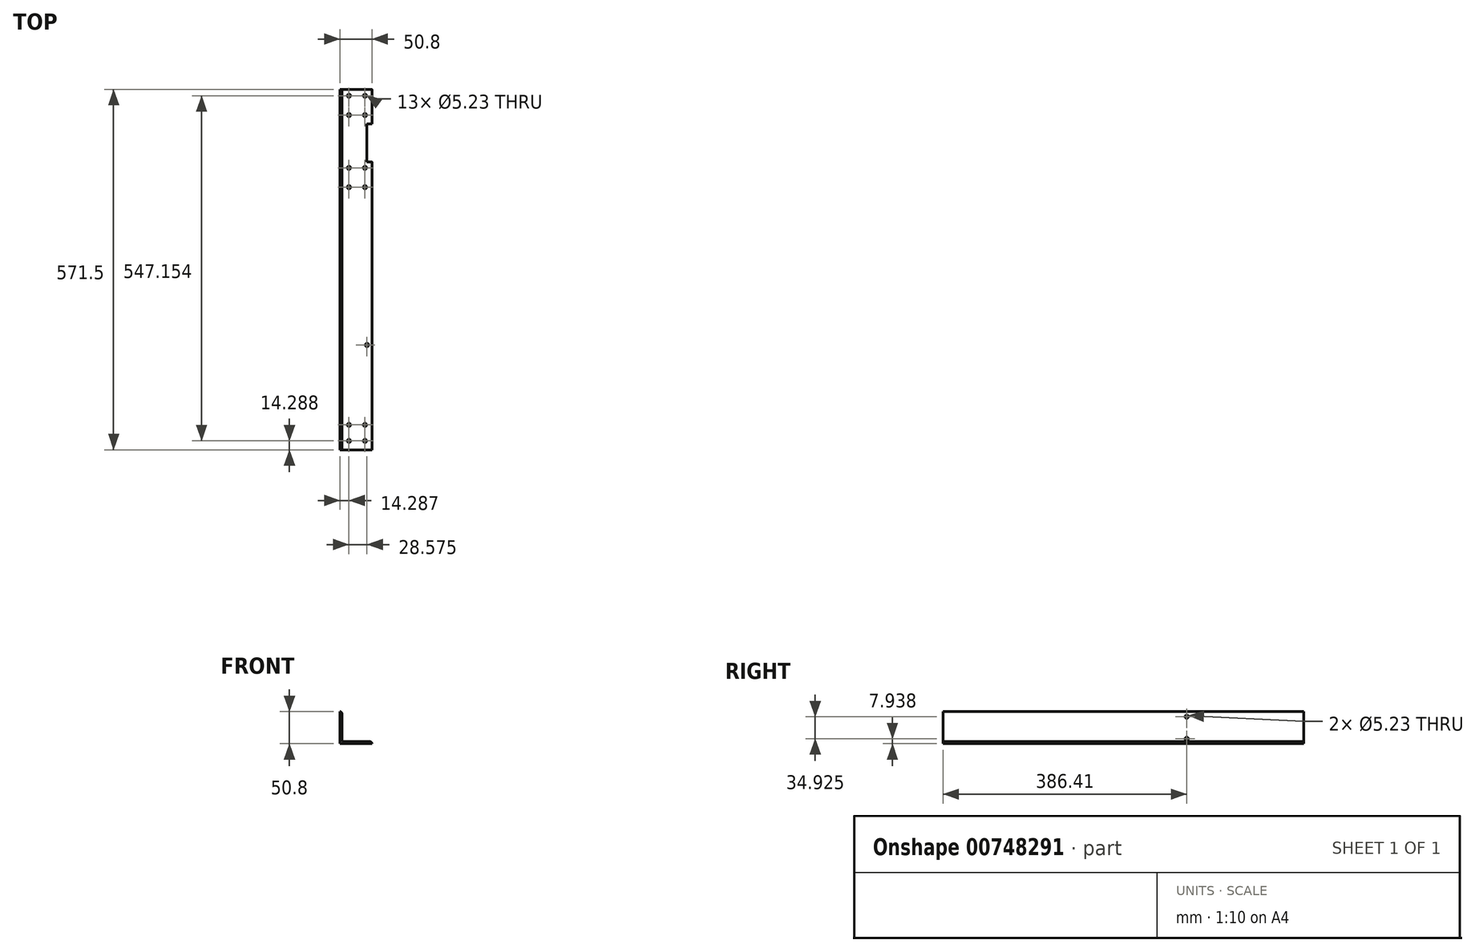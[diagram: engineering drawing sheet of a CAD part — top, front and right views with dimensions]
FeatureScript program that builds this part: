
annotation { "Feature Type Name" : "Feature", "Feature Type Description" : "" }
export const myFeature = defineFeature(function(context is Context, id is Id, definition is map)
    precondition{}
    {
        {
            var Q0;
            Q0=qCreatedBy(makeId("Front.planeOp"),FACE);
            var sketch = newSketch(context, id + "F0", { "sketchPlane" : qUnion([Q0])});
            skLineSegment(sketch, "E0", {"start": v(0, 0) * mm, "end": v(-50.8, 0) * mm});
            skLineSegment(sketch, "E1", {"start": v(-50.8, 0) * mm, "end": v(-50.8, 50.8) * mm});
            skLineSegment(sketch, "E2", {"start": v(-50.8, 50.8) * mm, "end": v(-50.8, 50.8) * mm});
            skLineSegment(sketch, "E3", {"start": v(-47.63, 47.63) * mm, "end": v(-47.63, 6.35) * mm});
            skLineSegment(sketch, "E4", {"start": v(-44.45, 3.18) * mm, "end": v(-3.18, 3.18) * mm});
            skLineSegment(sketch, "E5", {"start": v(0, 0) * mm, "end": v(0, 0) * mm});
            skPoint(sketch, "E6.visualSharp", {"position": v(-47.63, 3.18) * mm});
            skArc(sketch, "E6.filletArc", {"start": v(-47.63, 6.35) * mm, "mid": v(-46.7, 4.1) * mm, "end": v(-44.45, 3.18) * mm});
            skPoint(sketch, "E7.visualSharp", {"position": v(-47.63, 50.8) * mm});
            skArc(sketch, "E7.filletArc", {"start": v(-47.63, 47.63) * mm, "mid": v(-48.55, 49.87) * mm, "end": v(-50.8, 50.8) * mm});
            skPoint(sketch, "E8.visualSharp", {"position": v(0, 3.18) * mm});
            skArc(sketch, "E8.filletArc", {"start": v(0, 0) * mm, "mid": v(-0.93, 2.25) * mm, "end": v(-3.18, 3.18) * mm});
            skSolve(sketch);
        }
        {
            var Q0;
            Q0=qSketchRegion(id+"F0",true);
            extrude(context, id + "F1", {"entities" : qUnion([Q0]), "depth" : 571.5 * mm, "offsetDistance" : 25.4 * mm});
        }
        {
            var Q0;
            Q0=makeQuery(id+"F1.opExtrude","SWEPT_FACE",FACE,{"disambiguationData":[OSD([sQuery(id+"F0.wireOp",EDGE,"E4")])]});
            var sketch = newSketch(context, id + "F2", { "sketchPlane" : qUnion([Q0])});
            skLineSegment(sketch, "E9", {"start": v(-23.81, -571.5) * mm, "end": v(-23.81, 0) * mm, "construction": true});
            skLineSegment(sketch, "E10", {"start": v(-3.17, -557.21) * mm, "end": v(-44.45, -557.21) * mm, "construction": true});
            skCircle(sketch, "E11", {"center": v(-36.51, -557.21) * mm, "radius": 2.62 * mm});
            skLineSegment(sketch, "E12.0", {"start": v(-44.45, -10.06) * mm, "end": v(-3.17, -10.06) * mm, "construction": true});
            skLineSegment(sketch, "E13.0", {"start": v(-44.45, -40.74) * mm, "end": v(-3.17, -40.74) * mm, "construction": true});
            skCircle(sketch, "E14", {"center": v(-36.51, -40.74) * mm, "radius": 2.62 * mm});
            skCircle(sketch, "E15", {"center": v(-36.51, -10.06) * mm, "radius": 2.62 * mm});
            skLineSegment(sketch, "E16.0", {"start": v(-44.45, -124.4) * mm, "end": v(-3.17, -124.4) * mm, "construction": true});
            skLineSegment(sketch, "E17.0", {"start": v(-44.45, -155.1) * mm, "end": v(-3.17, -155.1) * mm, "construction": true});
            skCircle(sketch, "E18", {"center": v(-36.51, -124.4) * mm, "radius": 2.62 * mm});
            skCircle(sketch, "E19", {"center": v(-36.51, -155.1) * mm, "radius": 2.62 * mm});
            skLineSegment(sketch, "E20", {"start": v(-36.51, 0) * mm, "end": v(-36.51, -571.5) * mm, "construction": true});
            skLineSegment(sketch, "E21", {"start": v(-44.45, -531.81) * mm, "end": v(-3.17, -531.81) * mm, "construction": true});
            skLineSegment(sketch, "E22", {"start": v(-11.11, -571.5) * mm, "end": v(-11.11, 0) * mm, "construction": true});
            skCircle(sketch, "E23", {"center": v(-11.11, -40.74) * mm, "radius": 2.62 * mm});
            skCircle(sketch, "E24", {"center": v(-11.11, -10.06) * mm, "radius": 2.62 * mm});
            skCircle(sketch, "E25", {"center": v(-11.11, -155.1) * mm, "radius": 2.62 * mm});
            skCircle(sketch, "E26", {"center": v(-11.11, -124.4) * mm, "radius": 2.62 * mm});
            skCircle(sketch, "E27", {"center": v(-36.51, -531.81) * mm, "radius": 2.62 * mm});
            skCircle(sketch, "E28", {"center": v(-11.11, -531.81) * mm, "radius": 2.62 * mm});
            skCircle(sketch, "E29", {"center": v(-11.11, -557.21) * mm, "radius": 2.62 * mm});
            skLineSegment(sketch, "E30.bottom", {"start": v(-8.09, -54.7) * mm, "end": v(5.76, -54.7) * mm});
            skLineSegment(sketch, "E30.top", {"start": v(-8.09, -114.93) * mm, "end": v(5.76, -114.93) * mm});
            skLineSegment(sketch, "E30.left", {"start": v(-8.09, -54.7) * mm, "end": v(-8.09, -114.93) * mm});
            skLineSegment(sketch, "E30.right", {"start": v(5.76, -54.7) * mm, "end": v(5.76, -114.93) * mm});
            skLineSegment(sketch, "E31", {"start": v(-7.94, -571.5) * mm, "end": v(-7.94, 0) * mm, "construction": true});
            skCircle(sketch, "E32", {"center": v(-7.94, -405.18) * mm, "radius": 2.62 * mm});
            skLineSegment(sketch, "E33", {"start": v(-44.45, -528.65) * mm, "end": v(-3.17, -528.65) * mm, "construction": true});
            skSolve(sketch);
        }
        {
            var Q0;
            Q0=qSketchRegion(id+"F2",true);
            extrude(context, id + "F3", {"entities" : qUnion([Q0]), "operationType" : NewBodyOperationType.REMOVE, "endBound" : BoundingType.THROUGH_ALL, "oppositeDirection" : true, "depth" : 25.4 * mm, "offsetDistance" : 25.4 * mm});
        }
        {
            var Q0;
            Q0=makeQuery(id+"F1.opExtrude","SWEPT_FACE",FACE,{"disambiguationData":[OSD([sQuery(id+"F0.wireOp",EDGE,"E1")])]});
            var sketch = newSketch(context, id + "F4", { "sketchPlane" : qUnion([Q0])});
            skLineSegment(sketch, "E34", {"start": v(571.5, 7.94) * mm, "end": v(0, 7.94) * mm, "construction": true});
            skPoint(sketch, "E34.endSnap0", {"position": v(0, 25.4) * mm});
            skLineSegment(sketch, "E35", {"start": v(185.09, 0) * mm, "end": v(185.09, 50.8) * mm, "construction": true});
            skCircle(sketch, "E36", {"center": v(185.09, 7.94) * mm, "radius": 2.62 * mm});
            skLineSegment(sketch, "E37", {"start": v(0, 42.86) * mm, "end": v(571.5, 42.86) * mm, "construction": true});
            skCircle(sketch, "E38", {"center": v(185.09, 42.86) * mm, "radius": 2.62 * mm});
            skSolve(sketch);
        }
        {
            var Q0;
            Q0 = qSketchRegion(id + "F4", true);
            extrude(context, id + "F5", {"entities" : qUnion([Q0]), "operationType" : NewBodyOperationType.REMOVE, "endBound" : BoundingType.THROUGH_ALL, "oppositeDirection" : true, "depth" : 25.4 * mm, "offsetDistance" : 25.4 * mm});
        }
    });
